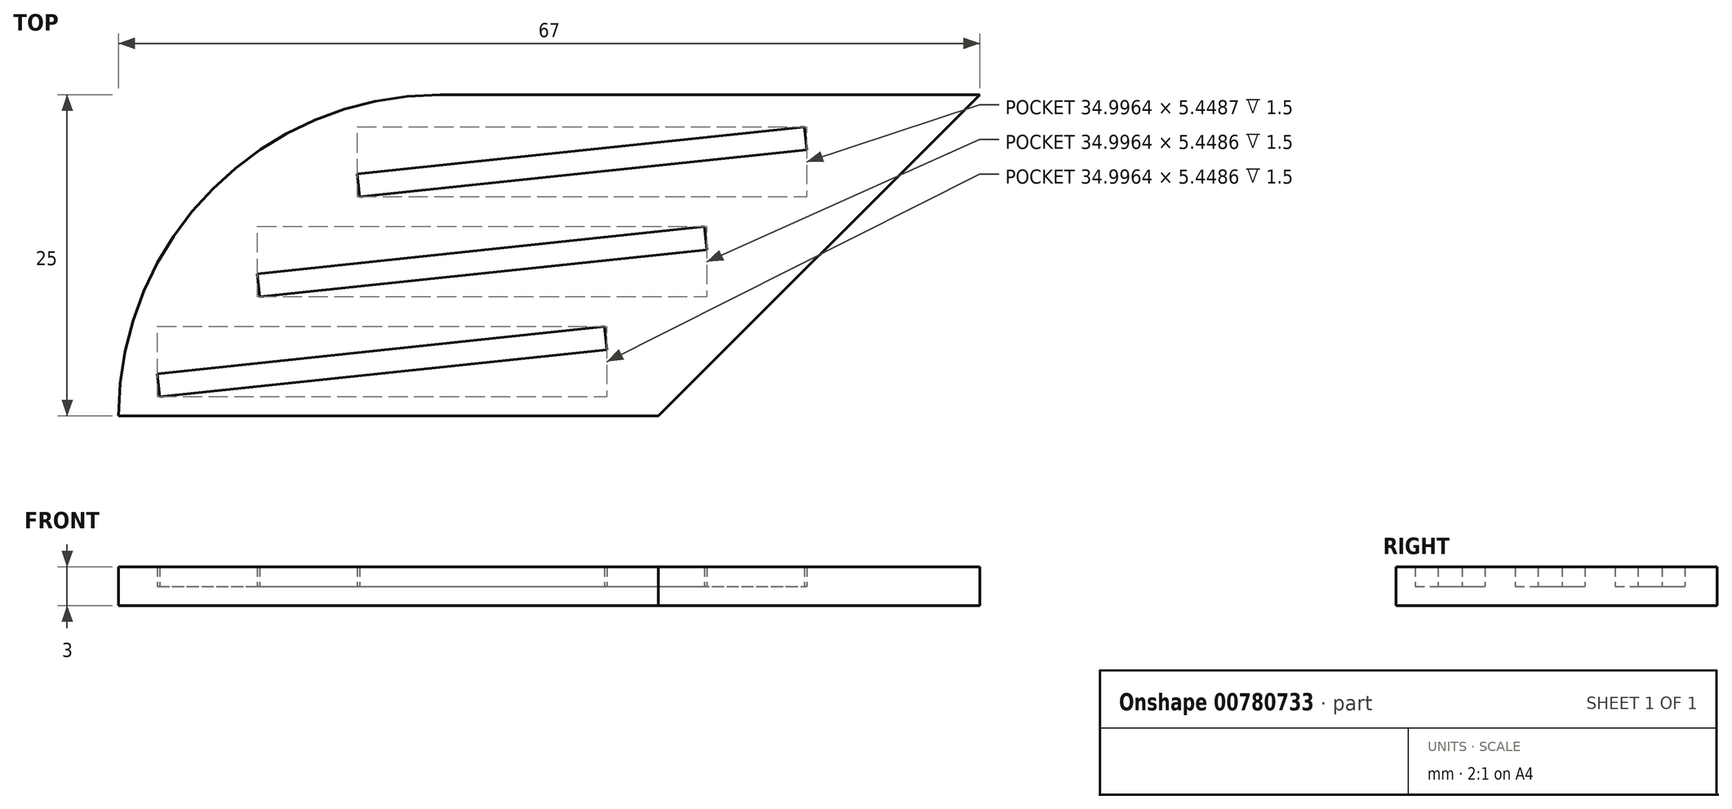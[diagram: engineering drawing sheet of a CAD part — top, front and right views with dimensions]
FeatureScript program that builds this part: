
annotation { "Feature Type Name" : "Feature", "Feature Type Description" : "" }
export const myFeature = defineFeature(function(context is Context, id is Id, definition is map)
    precondition{}
    {
        {
            var Q0;
            Q0=qCreatedBy(makeId("Top.planeOp"),FACE);
            var sketch = newSketch(context, id + "F0", { "sketchPlane" : qUnion([Q0])});
            skLineSegment(sketch, "E0.bottom", {"start": v(0, 0) * mm, "end": v(42, 0) * mm});
            skLineSegment(sketch, "E0.top", {"start": v(25, 25) * mm, "end": v(42, 25) * mm});
            skLineSegment(sketch, "E0.left", {"start": v(0, 0) * mm, "end": v(0, 0) * mm});
            skLineSegment(sketch, "E0.right", {"start": v(42, 0) * mm, "end": v(42, 25) * mm});
            skPoint(sketch, "E1.visualSharp", {"position": v(0, 25) * mm});
            skArc(sketch, "E1.filletArc", {"start": v(25, 25) * mm, "mid": v(7.32, 17.68) * mm, "end": v(0, 0) * mm});
            skLineSegment(sketch, "E2", {"start": v(42, 25) * mm, "end": v(67, 25) * mm});
            skLineSegment(sketch, "E3", {"start": v(67, 25) * mm, "end": v(42, 0) * mm});
            skSolve(sketch);
        }
        {
            var Q0;
            Q0 = qSketchRegion(id + "F0", true);
            extrude(context, id + "F1", {"entities" : qUnion([Q0]), "depth" : 3 * mm, "offsetDistance" : 25 * mm});
        }
        {
            var Q0;
            Q0=qCreatedBy(makeId("Top.planeOp"),FACE);
            var sketch = newSketch(context, id + "F2", { "sketchPlane" : qUnion([Q0])});
            skLineSegment(sketch, "E4.bottom", {"start": v(3.2, 1.5) * mm, "end": v(38, 5.16) * mm});
            skLineSegment(sketch, "E4.top", {"start": v(3, 3.3) * mm, "end": v(37.81, 6.95) * mm});
            skLineSegment(sketch, "E4.left", {"start": v(3.2, 1.5) * mm, "end": v(3, 3.3) * mm});
            skLineSegment(sketch, "E4.right", {"start": v(38, 5.16) * mm, "end": v(37.81, 6.95) * mm});
            skLineSegment(sketch, "E5.0.1.0", {"start": v(10.97, 9.28) * mm, "end": v(10.78, 11.07) * mm});
            skLineSegment(sketch, "E5.0.1.1", {"start": v(10.78, 11.07) * mm, "end": v(45.6, 14.73) * mm});
            skLineSegment(sketch, "E5.0.1.2", {"start": v(10.97, 9.28) * mm, "end": v(45.78, 12.94) * mm});
            skLineSegment(sketch, "E5.0.1.3", {"start": v(45.78, 12.94) * mm, "end": v(45.6, 14.73) * mm});
            skLineSegment(sketch, "E5.0.2.0", {"start": v(18.75, 17.06) * mm, "end": v(18.56, 18.85) * mm});
            skLineSegment(sketch, "E5.0.2.1", {"start": v(18.56, 18.85) * mm, "end": v(53.37, 22.5) * mm});
            skLineSegment(sketch, "E5.0.2.2", {"start": v(18.75, 17.06) * mm, "end": v(53.56, 20.71) * mm});
            skLineSegment(sketch, "E5.0.2.3", {"start": v(53.56, 20.71) * mm, "end": v(53.37, 22.5) * mm});
            skLineSegment(sketch, "E5.direction1", {"start": v(3.2, 1.5) * mm, "end": v(38.14, 1.5) * mm, "construction": true});
            skLineSegment(sketch, "E5.direction2", {"start": v(3.2, 1.5) * mm, "end": v(10.97, 9.28) * mm, "construction": true});
            skSolve(sketch);
        }
        {
            var Q0;
            Q0 = qSketchRegion(id + "F2", true);
            extrude(context, id + "F3", {"entities" : qUnion([Q0]), "operationType" : NewBodyOperationType.REMOVE, "depth" : 160 * mm, "offsetDistance" : 25 * mm, "hasSecondDirection" : true, "secondDirectionOppositeDirection" : false, "secondDirectionDepth" : 1.5 * mm});
        }
    });
